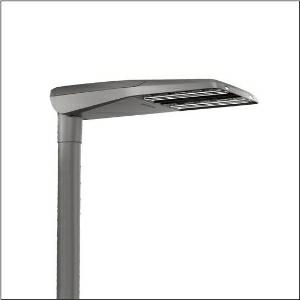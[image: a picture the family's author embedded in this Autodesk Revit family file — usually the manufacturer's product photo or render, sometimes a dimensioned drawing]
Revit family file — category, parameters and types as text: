
# Revit family: streetlight_sl_11_iq_midi___st1_0st0_5_5xc3j51g08me_56cc
name_source: partatom
category: Lighting Fixtures
units: mm (PartAtom-declared; Revit-internal decimal feet)

## family parameters
Cut with Voids When Loaded = No
Host = Face
Light Source = No
Part Type = Normal
Room Calculation Point = No
Round Connector Dimension = Use Diameter
Shared = No

## types (1)
- --- (1 x LED, 17640 lm, 122.6 W, 3000K)
    Apparent Load = 123 VA
    CIE Flux Codes = 35 68 96 100 100
    Color Rendering = 70
    Color Temperature = 3000K
    Default Elevation = 1800 mm
    Description = Streetlight SL 11 iQ midi, mast luminaire, primary light control with 3 zone facetted reflector, of plastic, silver coated, highly specular, primary optical cover: cover, of PMMA, transparent, light distribution: ST1.0ST0.5, light emission: direct distribution, primary light characteristic: asymmetric, installation type: post-top, side-entry, lamps: LED, High Power LED, rated values: 17.640lm | 122,6W | 143,9lm/W (begin service life); end service life: 17.640lm | 130,2W; at 50% lumin. flux: 8.820lm | 56,1W | 157,2lm/W, colour temperature: 3000K, colour rendering: CRI > 70, light colour: 730, light setting 1 begin service life: 100% | 17.640lm | 122,6W | 143,9lm/W | 3.000K, light setting 1 end service life: 130,2W, further light settings possible, control: Street-Remote, Auto-Match, Temp-Guard, Lumen-Switch, Night-Set, Smart-Wire, Light-Fading, Desk-Remote (wireless, voltage-free reading and setting of iQ features in the workshop via application-optimized NFC function/RFID function), optimised constant luminous flux control (CLO 2.0), pre-setting: linear dimming characteristic, with cable H07RN-F 5x 1.5mm², mains connection: 230..240V, AC, 50/60Hz, connection cable pre-assembled, cable length: 12,5m, luminaire housing, of diecast aluminium, powder-coated, SITECO metallic grey (DB 702S), please order mast flange separately, inclination adjustable without tools: 0°, 5°, 10°, 15° (post-top) | 0°, -5°, -10°, -15° (side-entry), sealing non-destructively replaceable, multi-level sealing system, length: 780mm, width: 376mm, height: 118mm, mast flange for spigot size: 42mm (side-entry): 5XC10008XM4, 60/48mm (side-entry/post-top): 5XC10108XM2, 76/60mm (side-entry/post-top): 5XC10108XM1, equipment: Power, protection rating (complete): IP66, insulation class (complete): insulation class II (safety insulation), certification: CE, ENEC, ENEC+, VDE, impact resistance: IK10, permissible operating ambient temperature for outdoor applications: -25..+50°C, standard-compliant lighting for roads and squares, Environmental Product Declaration (EPD) tested and certified by an independent institute, packaging unit: 1 piece

Light Distribution: ST1.0ST0.5
    Height = 118 mm
    Lamp = 1 x LED
    Lamp Light Flux = 17640 lm
    Lamp Power = 122.6 W
    Lamp count = 1
    Length = 780 mm
    Luminous efficacy = 144 lm/W
    Manufacturer = Siteco
    ModVariant = No
    Model = 5XC3J51G08ME
    Number of Poles = 1
    OnlyDefault = Yes
    Power Factor = 1
    Product Name = Streetlight SL 11 iQ midi | ST1.0ST0.5
    Product group = mast luminaire | pylon top
    ProductGroupID = 6100
    Protection Class = Protection class II
    Protection Degree = IP 66
    RLX_Detail_Level = 1
    RLX_Emergency_Light_Flux = 0 lm
    RLX_Emergency_Type = 0
    RLX_Emergency_Type_DB = No
    RlxData = <blob elided: 70889 chars, md5=1c2c0dfd>
    Socket = socket
    Standby Power = 0 W
    System Light Flux = 17640 lm
    System Power = 123 W
    Type Comments = factory setting: luminous flux: 100 % | dim-lin: 254 | 552 mA
    Type Image = l_1005960.jpg
    URL = http://relux.com
    VarID = @adj_027581
    Voltage = 0 V
    Weight = 0.00 kg
    Width = 376 mm

## geometry (parser evidence)
native form markers: Blend x4, Sweep x10
no freeform markers — native parametric forms only
